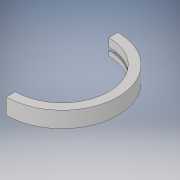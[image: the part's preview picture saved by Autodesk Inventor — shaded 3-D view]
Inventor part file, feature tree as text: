
AUTODESK INVENTOR PART (.ipt)
format: ipt  version: 2017 (Build 210142000, 142)  size: 139,776 bytes
history: native  units: in
note: dims shown in document units (in); Inventor stores cm internally (conversion verified against a paired STEP export)
features: revolve x1, sketch x1
ambient origin geometry x8: Origin, YZ Plane, XZ Plane, XY Plane, X Axis, Y Axis, Z Axis, Center Point
bodies: Solid1 (feature_tree)
feature tree (2):
  revolve  "Revolution1"  [1 undecoded]
  sketch  "Sketch1"  dims[d1=0.9911in d2=5.1195in d3=1.7489in d4=0.0in d5=0.0625in d6=0.0625in d7=0.0625in d8=0.0625in d9=0.7182in d10=0.3125in d11=0.1562in d12=180.0deg]
note: 1 required parameter value undecoded (feature->parameter linkage not recoverable at this tier; creation-order binding heuristic only, values carry confidence <= 0.55)
